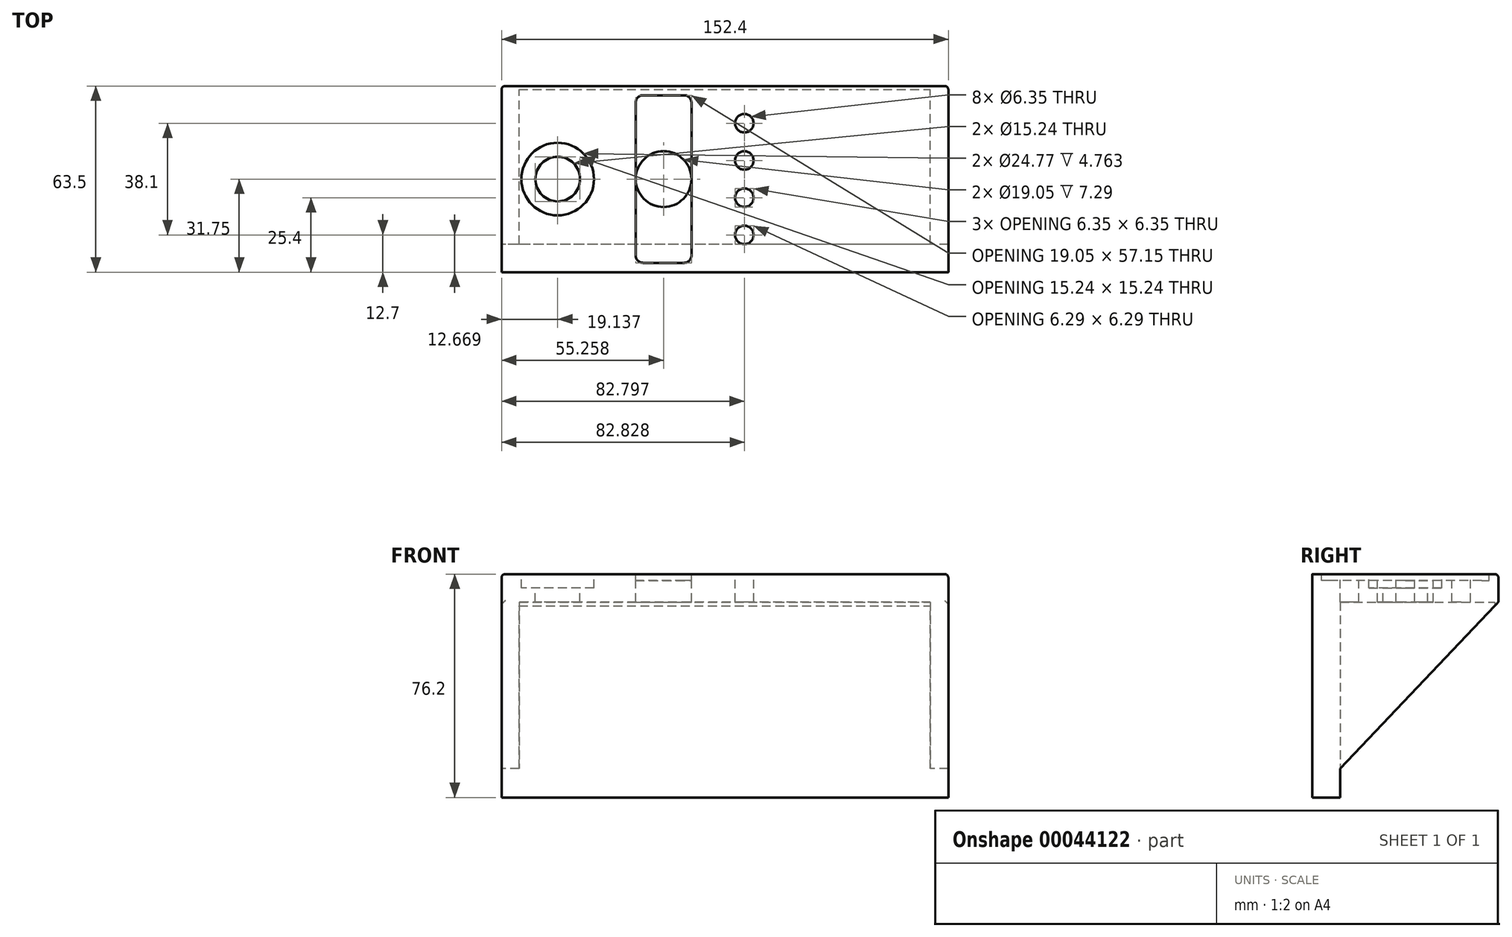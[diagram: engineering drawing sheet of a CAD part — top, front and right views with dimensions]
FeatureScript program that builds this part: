
annotation { "Feature Type Name" : "Feature", "Feature Type Description" : "" }
export const myFeature = defineFeature(function(context is Context, id is Id, definition is map)
    precondition{}
    {
        {
            var Q0;
            Q0=qCreatedBy(makeId("Right.planeOp"),FACE);
            var sketch = newSketch(context, id + "F0", { "sketchPlane" : qUnion([Q0])});
            skLineSegment(sketch, "E0", {"start": v(0, 0) * mm, "end": v(0, -76.2) * mm});
            skLineSegment(sketch, "E1", {"start": v(0, -76.2) * mm, "end": v(9.53, -76.2) * mm});
            skLineSegment(sketch, "E2", {"start": v(9.53, -76.2) * mm, "end": v(9.52, -66.28) * mm});
            skLineSegment(sketch, "E3", {"start": v(63.5, 0) * mm, "end": v(0, 0) * mm});
            skLineSegment(sketch, "E4", {"start": v(63.5, 0) * mm, "end": v(63.5, -9.52) * mm});
            skLineSegment(sketch, "E5", {"start": v(63.5, -9.52) * mm, "end": v(9.52, -66.28) * mm});
            skSolve(sketch);
        }
        {
            var Q0;
            Q0=makeQuery(id+"F0.imprint","IMPRINT",FACE,{"disambiguationData":[TD([[makeQuery(id+"F0.imprint","IMPRINT",EDGE,{"derivedFrom":sQuery(id+"F0.wireOp",EDGE,"E0")}),1.0]])]});
            extrude(context, id + "F1", {"entities" : qUnion([Q0]), "depth" : 152.4 * mm});
        }
        {
            var Q0;
            Q0=makeQuery(id+"F1.opExtrude","SWEPT_FACE",FACE,{"disambiguationData":[OSD([sQuery(id+"F0.wireOp",EDGE,"E1")])]});
            var sketch = newSketch(context, id + "F2", { "sketchPlane" : qUnion([Q0])});
            skLineSegment(sketch, "E6.bottom", {"start": v(5.99, -9.53) * mm, "end": v(146.25, -9.53) * mm});
            skLineSegment(sketch, "E6.top", {"start": v(5.99, -62.28) * mm, "end": v(146.25, -62.28) * mm});
            skLineSegment(sketch, "E6.left", {"start": v(5.99, -9.53) * mm, "end": v(5.99, -62.28) * mm});
            skLineSegment(sketch, "E6.right", {"start": v(146.25, -9.53) * mm, "end": v(146.25, -62.28) * mm});
            skSolve(sketch);
        }
        {
            var Q0;
            Q0 = qSketchRegion(id + "F2", true);
            var Q1;
            Q1=makeQuery(id+"F1.opExtrude","SWEPT_FACE",FACE,{"disambiguationData":[OSD([sQuery(id+"F0.wireOp",EDGE,"92394834-b365-4c2c-81ca-d6f6e1137bfa")])]});
            extrude(context, id + "F3", {"entities" : qUnion([Q0]), "operationType" : NewBodyOperationType.REMOVE, "oppositeDirection" : true, "endBoundEntityFace" : qUnion([Q1]), "depth" : 66.69 * mm});
        }
        {
            var Q0;
            Q0=makeQuery(id+"F1.opExtrude","SWEPT_FACE",FACE,{"disambiguationData":[OSD([sQuery(id+"F0.wireOp",EDGE,"E3")])]});
            var sketch = newSketch(context, id + "F4", { "sketchPlane" : qUnion([Q0])});
            skCircle(sketch, "E7", {"center": v(19.14, 31.75) * mm, "radius": 7.62 * mm});
            skCircle(sketch, "E8", {"center": v(19.14, 31.75) * mm, "radius": 12.38 * mm});
            skLineSegment(sketch, "E9", {"start": v(0, 31.75) * mm, "end": v(152.4, 31.75) * mm, "construction": true});
            skCircle(sketch, "E10", {"center": v(55.26, 31.75) * mm, "radius": 9.53 * mm});
            skLineSegment(sketch, "E11.rect.bottom", {"start": v(62.24, 60.32) * mm, "end": v(48.27, 60.32) * mm});
            skLineSegment(sketch, "E11.rect.top", {"start": v(62.24, 3.17) * mm, "end": v(48.27, 3.17) * mm});
            skLineSegment(sketch, "E11.rect.left", {"start": v(64.78, 57.78) * mm, "end": v(64.78, 5.71) * mm});
            skLineSegment(sketch, "E11.rect.right", {"start": v(45.73, 57.78) * mm, "end": v(45.73, 5.71) * mm});
            skCircle(sketch, "E12", {"center": v(82.8, 12.7) * mm, "radius": 2.54 * mm});
            skCircle(sketch, "E13.0.1.0", {"center": v(82.8, 25.4) * mm, "radius": 2.54 * mm});
            skCircle(sketch, "E13.0.2.0", {"center": v(82.8, 38.1) * mm, "radius": 2.54 * mm});
            skCircle(sketch, "E13.0.3.0", {"center": v(82.8, 50.8) * mm, "radius": 2.54 * mm});
            skLineSegment(sketch, "E13.direction1", {"start": v(82.8, 12.7) * mm, "end": v(108, 12.7) * mm, "construction": true});
            skLineSegment(sketch, "E13.direction2", {"start": v(82.8, 12.7) * mm, "end": v(82.8, 25.4) * mm, "construction": true});
            skLineSegment(sketch, "E14", {"start": v(82.8, 50.8) * mm, "end": v(82.8, 12.7) * mm, "construction": true});
            skPoint(sketch, "E15", {"position": v(82.8, 31.75) * mm});
            skPoint(sketch, "E16.visualSharp", {"position": v(64.78, 60.32) * mm});
            skArc(sketch, "E16.filletArc", {"start": v(64.78, 57.78) * mm, "mid": v(64.04, 59.58) * mm, "end": v(62.24, 60.32) * mm});
            skPoint(sketch, "E17.visualSharp", {"position": v(64.78, 3.17) * mm});
            skArc(sketch, "E17.filletArc", {"start": v(62.24, 3.17) * mm, "mid": v(64.04, 3.92) * mm, "end": v(64.78, 5.71) * mm});
            skPoint(sketch, "E18.visualSharp", {"position": v(45.73, 3.17) * mm});
            skArc(sketch, "E18.filletArc", {"start": v(45.73, 5.71) * mm, "mid": v(46.48, 3.92) * mm, "end": v(48.27, 3.17) * mm});
            skPoint(sketch, "E19.visualSharp", {"position": v(45.73, 60.32) * mm});
            skArc(sketch, "E19.filletArc", {"start": v(48.27, 60.32) * mm, "mid": v(46.48, 59.58) * mm, "end": v(45.73, 57.78) * mm});
            skSolve(sketch);
        }
        {
            var Q0;
            Q0=makeQuery(id+"F4.imprint","IMPRINT",FACE,{"disambiguationData":[TD([[makeQuery(id+"F4.imprint","IMPRINT",EDGE,{"derivedFrom":sQuery(id+"F4.wireOp",EDGE,"E7")}),1.0]])]});
            var Q1;
            Q1=sQuery(id+"F4.wireOp",EDGE,"E7");
            extrude(context, id + "F5", {"entities" : qUnion([Q0]), "operationType" : NewBodyOperationType.REMOVE, "surfaceEntities" : qUnion([Q1]), "oppositeDirection" : true, "depth" : 25.4 * mm});
        }
        {
            var Q0;
            Q0=makeQuery(id+"F4.imprint","IMPRINT",FACE,{"disambiguationData":[TD([[makeQuery(id+"F4.imprint","IMPRINT",EDGE,{"derivedFrom":sQuery(id+"F4.wireOp",EDGE,"E7")}),-1.0]])]});
            var Q1;
            Q1=sQuery(id+"F4.wireOp",EDGE,"E7");
            extrude(context, id + "F6", {"entities" : qUnion([Q0]), "operationType" : NewBodyOperationType.REMOVE, "surfaceEntities" : qUnion([Q1]), "oppositeDirection" : true, "depth" : 4.76 * mm});
        }
        {
            var Q0;
            {var subQ0=sQuery(id+"F4.wireOp",EDGE,"E10");var subQ2=makeQuery(id+"F4.imprint","INTERSECT",VERTEX,{"derivedFrom":[subQ0,sQuery(id+"F4.wireOp",EDGE,"E11.rect.left")]});Q0=makeQuery(id+"F4.imprint","IMPRINT",FACE,{"disambiguationData":[TD([[makeQuery(id+"F4.imprint","IMPRINT",EDGE,{"disambiguationData":[TD([[subQ2,-1.0]])],"derivedFrom":subQ0}),1.0]])]});}
            var Q1;
            Q1=sQuery(id+"F4.wireOp",EDGE,"E10");
            extrude(context, id + "F7", {"entities" : qUnion([Q0]), "operationType" : NewBodyOperationType.REMOVE, "surfaceEntities" : qUnion([Q1]), "oppositeDirection" : true, "depth" : 25.4 * mm});
        }
        {
            var Q0;
            {var subQ3=sQuery(id+"F4.wireOp",EDGE,"E11.rect.bottom");Q0=makeQuery(id+"F4.imprint","IMPRINT",FACE,{"disambiguationData":[TD([[makeQuery(id+"F4.imprint","IMPRINT",EDGE,{"derivedFrom":subQ3}),1.0]])]});}
            extrude(context, id + "F8", {"entities" : qUnion([Q0]), "operationType" : NewBodyOperationType.REMOVE, "oppositeDirection" : true, "depth" : 2.22 * mm});
        }
        {
            var Q0;
            {var subQ3=sQuery(id+"F4.wireOp",EDGE,"E11.rect.top");Q0=makeQuery(id+"F4.imprint","IMPRINT",FACE,{"disambiguationData":[TD([[makeQuery(id+"F4.imprint","IMPRINT",EDGE,{"derivedFrom":subQ3}),-1.0]])]});}
            extrude(context, id + "F9", {"entities" : qUnion([Q0]), "operationType" : NewBodyOperationType.REMOVE, "oppositeDirection" : true, "depth" : 2.22 * mm});
        }
        {
            var Q0;
            Q0=sQuery(id+"F4.wireOp",VERTEX,"E14.start");
            var Q1;
            Q1=sQuery(id+"F4.wireOp",VERTEX,"E13.0.2.0.center");
            var Q2;
            Q2=sQuery(id+"F4.wireOp",VERTEX,"E13.0.1.0.center");
            var Q3;
            Q3=sQuery(id+"F4.wireOp",VERTEX,"E12.center");
            var Q4;
            Q4=makeQuery(id+"F1.opExtrude","SWEPT_BODY",BODY,{"disambiguationData":[OSD([sQuery(id+"F0.wireOp",EDGE,"E0"),sQuery(id+"F0.wireOp",EDGE,"E1"),sQuery(id+"F0.wireOp",EDGE,"E2"),sQuery(id+"F0.wireOp",EDGE,"E3"),sQuery(id+"F0.wireOp",EDGE,"E4"),sQuery(id+"F0.wireOp",EDGE,"E5")])]});
            hole(context, id + "F10", {"style" : HoleStyle.SIMPLE, "holeDiameter" : 6.35 * mm, "endStyle" : HoleEndStyle.THROUGH, "locations" : qUnion([Q0, Q1, Q2, Q3]), "scope" : qUnion([Q4])});
        }
        {
            var Q0;
            Q0=makeQuery(id+"F1.opExtrude","CAP_EDGE",EDGE,{"disambiguationData":[OSD([sQuery(id+"F0.wireOp",EDGE,"E3")])],"isStart":false});
            var Q1;
            Q1=makeQuery(id+"F1.opExtrude","SWEPT_EDGE",EDGE,{"disambiguationData":[OSD([sQuery(id+"F0.wireOp",EDGE,"E3"),sQuery(id+"F0.wireOp",EDGE,"E4")])]});
            var Q2;
            Q2=makeQuery(id+"F1.opExtrude","CAP_EDGE",EDGE,{"disambiguationData":[OSD([sQuery(id+"F0.wireOp",EDGE,"E3")])],"isStart":true});
            var Q3;
            Q3=makeQuery(id+"F1.opExtrude","CAP_EDGE",EDGE,{"disambiguationData":[OSD([sQuery(id+"F0.wireOp",EDGE,"E4")])],"isStart":true});
            var Q4;
            Q4=makeQuery(id+"F1.opExtrude","CAP_EDGE",EDGE,{"disambiguationData":[OSD([sQuery(id+"F0.wireOp",EDGE,"E4")])],"isStart":false});
            var Q5;
            Q5=makeQuery(id+"F1.opExtrude","SWEPT_EDGE",EDGE,{"disambiguationData":[OSD([sQuery(id+"F0.wireOp",EDGE,"E4"),sQuery(id+"F0.wireOp",EDGE,"E5")])]});
            fillet(context, id + "F11", {"entities" : qUnion([Q0, Q1, Q2, Q3, Q4, Q5]), "radius" : 1.27 * mm, "tangentPropagation" : true, "allowEdgeOverflow" : false});
        }
    });
